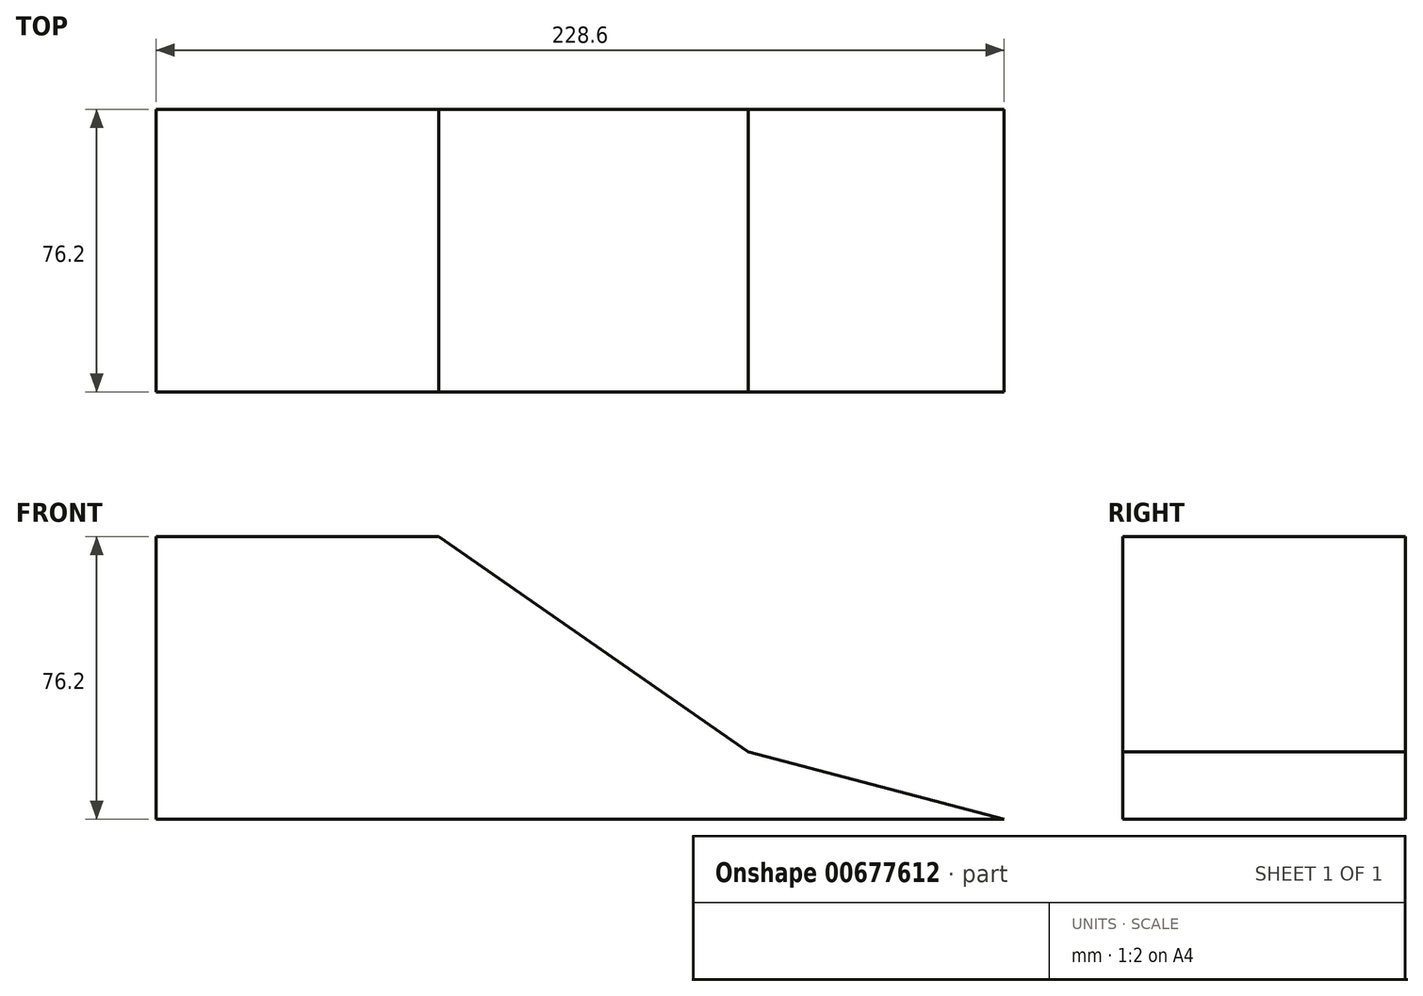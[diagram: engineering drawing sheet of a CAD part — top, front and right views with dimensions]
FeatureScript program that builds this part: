
annotation { "Feature Type Name" : "Feature", "Feature Type Description" : "" }
export const myFeature = defineFeature(function(context is Context, id is Id, definition is map)
    precondition{}
    {
        {
            var Q0;
            Q0=qCreatedBy(makeId("Front.planeOp"),FACE);
            var sketch = newSketch(context, id + "F0", { "sketchPlane" : qUnion([Q0])});
            skLineSegment(sketch, "E0", {"start": v(0, 0) * mm, "end": v(228.6, 0) * mm});
            skLineSegment(sketch, "E1", {"start": v(0, 0) * mm, "end": v(50.8, 0) * mm});
            skLineSegment(sketch, "E2", {"start": v(0, 0) * mm, "end": v(0, 76.2) * mm});
            skLineSegment(sketch, "E3", {"start": v(0, 76.2) * mm, "end": v(76.2, 76.2) * mm});
            skLineSegment(sketch, "E4", {"start": v(76.2, 76.2) * mm, "end": v(159.6, 18.16) * mm});
            skLineSegment(sketch, "E5", {"start": v(159.6, 18.16) * mm, "end": v(228.6, 0) * mm});
            skSolve(sketch);
        }
        {
            var Q0;
            Q0 = qSketchRegion(id + "F0", true);
            extrude(context, id + "F1", {"entities" : qUnion([Q0]), "depth" : 76.2 * mm, "offsetDistance" : 25.4 * mm});
        }
    });
